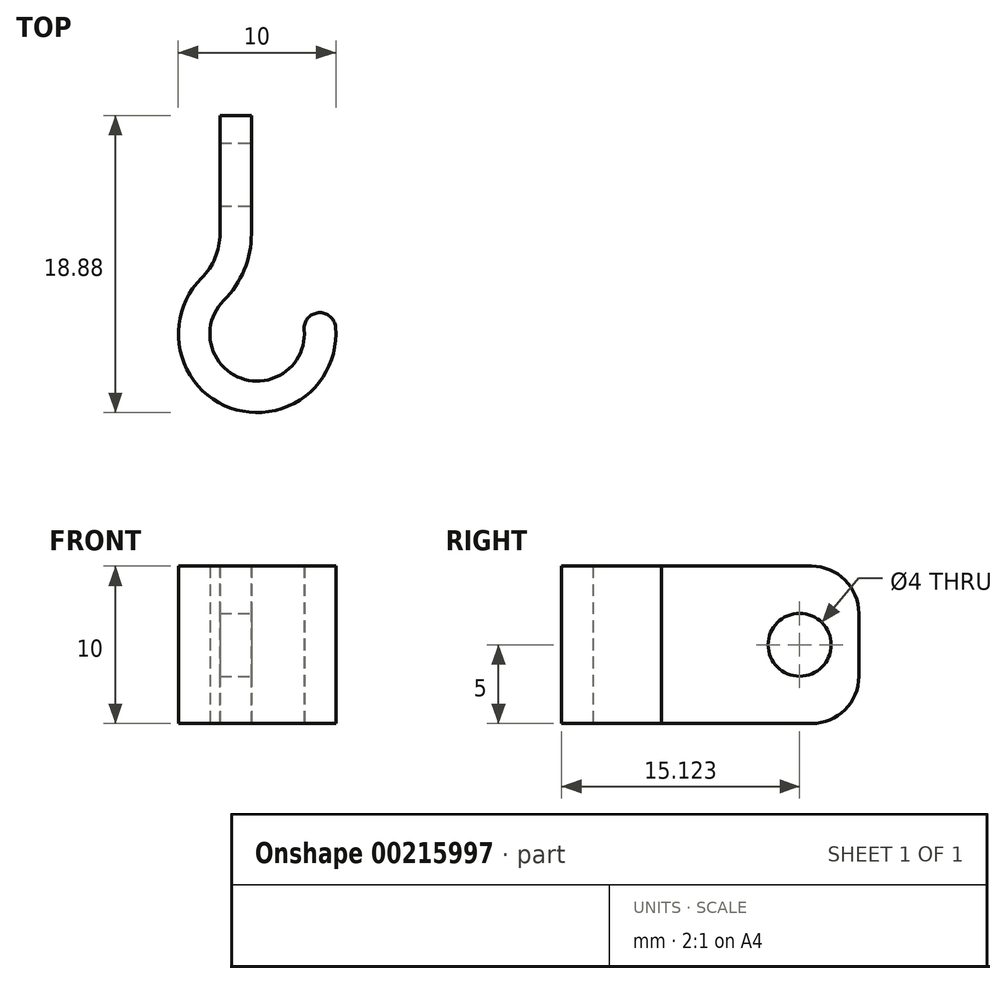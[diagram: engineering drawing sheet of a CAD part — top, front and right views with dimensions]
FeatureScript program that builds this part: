
annotation { "Feature Type Name" : "Feature", "Feature Type Description" : "" }
export const myFeature = defineFeature(function(context is Context, id is Id, definition is map)
    precondition{}
    {
        {
            var Q0;
            Q0=qCreatedBy(makeId("Top.planeOp"),FACE);
            var sketch = newSketch(context, id + "F0", { "sketchPlane" : qUnion([Q0])});
            skArc(sketch, "E0", {"start": v(-1.76, -11.76) * mm, "mid": v(-0.66, -16.7) * mm, "end": v(3.35, -13.62) * mm});
            skLineSegment(sketch, "E1", {"start": v(0, 0) * mm, "end": v(0, -7.51) * mm});
            skLineSegment(sketch, "E2", {"start": v(-1.76, -11.76) * mm, "end": v(-7.44, -17.44) * mm, "construction": true});
            skPoint(sketch, "E3.visualSharp", {"position": v(0, -10) * mm});
            skArc(sketch, "E3.filletArc", {"start": v(-1.76, -11.76) * mm, "mid": v(-0.46, -9.81) * mm, "end": v(0, -7.51) * mm});
            skLineSegment(sketch, "E4", {"start": v(8.9, -22.42) * mm, "end": v(-6, -7.51) * mm, "construction": true});
            skLineSegment(sketch, "E5", {"start": v(0.36, -13.88) * mm, "end": v(10.5, -13) * mm, "construction": true});
            skArc(sketch, "E6.0", {"start": v(-3.17, -10.34) * mm, "mid": v(-1.35, -18.58) * mm, "end": v(5.34, -13.44) * mm});
            skArc(sketch, "E6.1", {"start": v(-3.17, -10.34) * mm, "mid": v(-2.3, -9.05) * mm, "end": v(-2, -7.51) * mm});
            skLineSegment(sketch, "E6.2", {"start": v(-2, 0) * mm, "end": v(-2, -7.51) * mm});
            skLineSegment(sketch, "E7", {"start": v(-2, 0) * mm, "end": v(0, 0) * mm});
            skArc(sketch, "E8", {"start": v(3.35, -13.62) * mm, "mid": v(4.26, -12.53) * mm, "end": v(5.34, -13.44) * mm});
            skSolve(sketch);
        }
        {
            var Q0;
            Q0=makeQuery(id+"F0.imprint","IMPRINT",FACE,{"disambiguationData":[TD([[makeQuery(id+"F0.imprint","IMPRINT",EDGE,{"derivedFrom":sQuery(id+"F0.wireOp",EDGE,"E0")}),-1.0]])]});
            extrude(context, id + "F1", {"entities" : qUnion([Q0]), "depth" : 10 * mm});
        }
        {
            var Q0;
            Q0=makeQuery(id+"F1.opExtrude","CAP_EDGE",EDGE,{"disambiguationData":[OSD([sQuery(id+"F0.wireOp",EDGE,"E7")])],"isStart":false});
            var Q1;
            Q1=makeQuery(id+"F1.opExtrude","CAP_EDGE",EDGE,{"disambiguationData":[OSD([sQuery(id+"F0.wireOp",EDGE,"E7")])],"isStart":true});
            fillet(context, id + "F2", {"entities" : qUnion([Q0, Q1]), "radius" : 3 * mm, "tangentPropagation" : true, "allowEdgeOverflow" : false});
        }
        {
            var Q0;
            Q0=makeQuery(id+"F1.opExtrude","SWEPT_FACE",FACE,{"disambiguationData":[OSD([sQuery(id+"F0.wireOp",EDGE,"E1")])]});
            var sketch = newSketch(context, id + "F3", { "sketchPlane" : qUnion([Q0])});
            skPoint(sketch, "E9", {"position": v(-3.76, 5) * mm});
            skLineSegment(sketch, "E10", {"start": v(-7.51, 5) * mm, "end": v(0, 5) * mm, "construction": true});
            skSolve(sketch);
        }
        {
            var Q0;
            Q0=sQuery(id+"F3.wireOp",VERTEX,"E9");
            var Q1;
            Q1=makeQuery(id+"F1.opExtrude","SWEPT_BODY",BODY,{"disambiguationData":[OSD([sQuery(id+"F0.wireOp",EDGE,"E0"),sQuery(id+"F0.wireOp",EDGE,"E1"),sQuery(id+"F0.wireOp",EDGE,"E3.filletArc"),sQuery(id+"F0.wireOp",EDGE,"E6.0"),sQuery(id+"F0.wireOp",EDGE,"E6.1"),sQuery(id+"F0.wireOp",EDGE,"E6.2"),sQuery(id+"F0.wireOp",EDGE,"muziL5E5-Y0QJ-Vpg7-OY8A-YcXms5r5ZsRk"),sQuery(id+"F0.wireOp",EDGE,"e21d6fce-4bed-41fc-a4df-43e7c3783eb7")])]});
            hole(context, id + "F4", {"style" : HoleStyle.SIMPLE, "endStyle" : HoleEndStyle.THROUGH, "standardTappedOrClearance" : lookupTablePath({ "standard" : "Custom", "fit" : "Normal", "size" : "1/4", "type" : "Drilled" }), "standardBlindInLast" : lookupTablePath({ "fit" : "Free", "standard" : "Custom", "size" : "1/4", "type" : "Drilled" }), "holeDiameter" : 4 * mm, "startFromSketch" : true, "locations" : qUnion([Q0]), "scope" : qUnion([Q1]), "isTappedThrough" : true});
        }
    });
